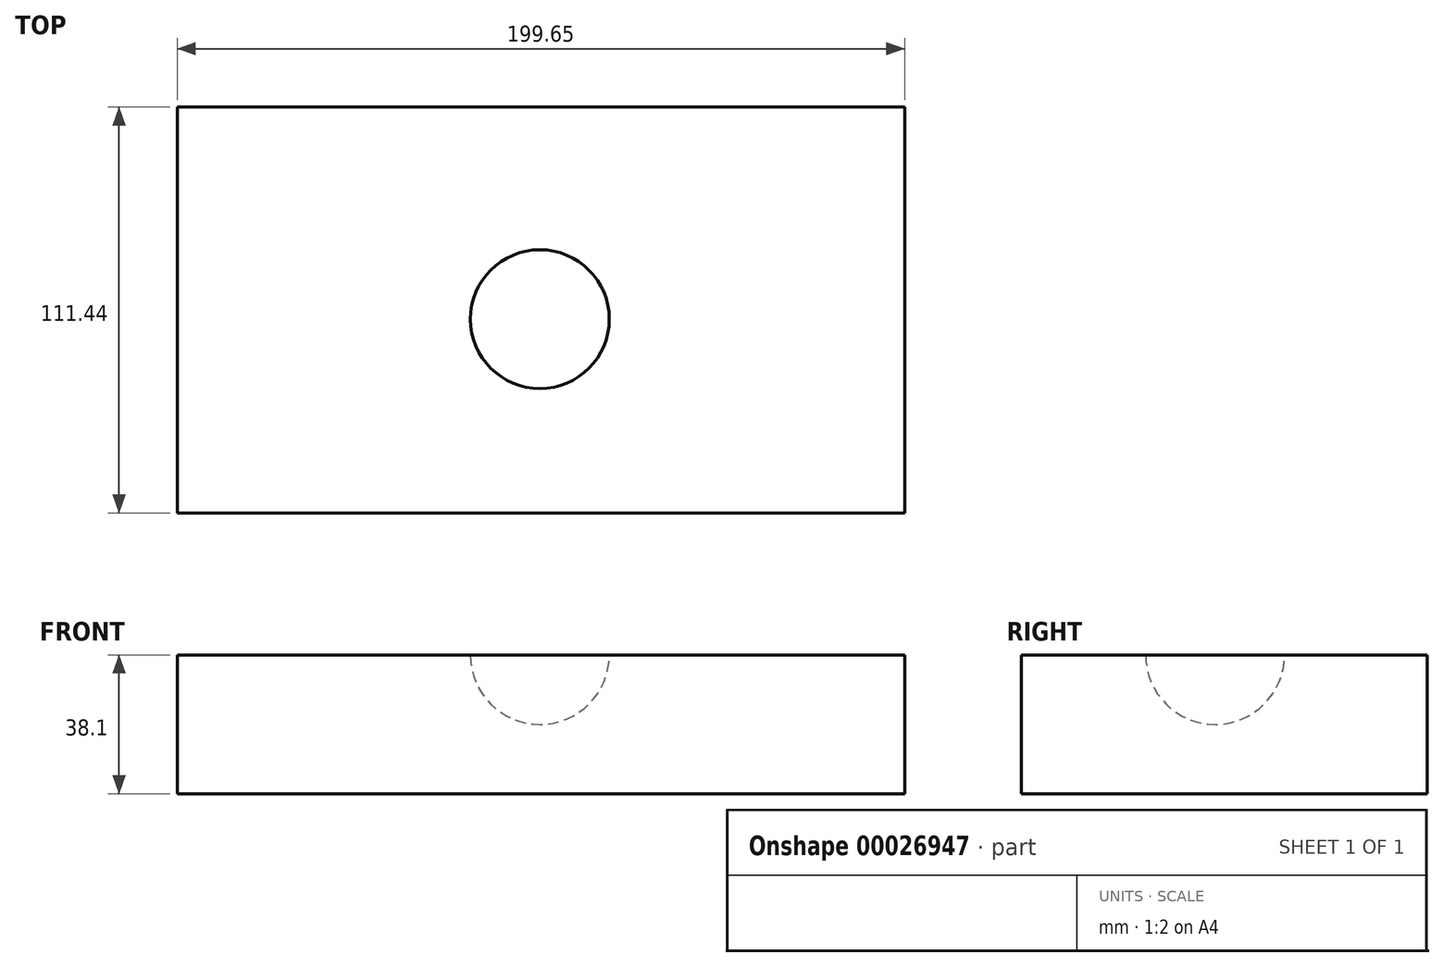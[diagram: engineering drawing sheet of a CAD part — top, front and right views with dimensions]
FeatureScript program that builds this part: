
annotation { "Feature Type Name" : "Feature", "Feature Type Description" : "" }
export const myFeature = defineFeature(function(context is Context, id is Id, definition is map)
    precondition{}
    {
        {
            var Q0;
            Q0=qCreatedBy(makeId("Top.planeOp"),FACE);
            var sketch = newSketch(context, id + "F0", { "sketchPlane" : qUnion([Q0])});
            skLineSegment(sketch, "E0.bottom", {"start": v(-99.53, 55.87) * mm, "end": v(100.12, 55.87) * mm});
            skLineSegment(sketch, "E0.top", {"start": v(-99.53, -55.57) * mm, "end": v(100.12, -55.57) * mm});
            skLineSegment(sketch, "E0.left", {"start": v(-99.53, 55.87) * mm, "end": v(-99.53, -55.57) * mm});
            skLineSegment(sketch, "E0.right", {"start": v(100.12, 55.87) * mm, "end": v(100.12, -55.57) * mm});
            skSolve(sketch);
        }
        {
            var Q0;
            Q0 = qSketchRegion(id + "F0", true);
            extrude(context, id + "F1", {"entities" : qUnion([Q0]), "depth" : 38.1 * mm});
        }
        {
            var Q0;
            Q0=qCreatedBy(makeId("Top.planeOp"),FACE);
            cPlane(context, id + "F2", {"entities" : qUnion([Q0]), "cplaneType" : CPlaneType.OFFSET, "offset" : 38.1 * mm, "width" : 152.4 * mm, "height" : 152.4 * mm});
        }
        {
            var Q0;
            Q0=qCreatedBy(id+"F2.planeOp",FACE);
            var sketch = newSketch(context, id + "F3", { "sketchPlane" : qUnion([Q0])});
            skLineSegment(sketch, "E1", {"start": v(0, 16.7) * mm, "end": v(0, -21.4) * mm});
            skArc(sketch, "E2", {"start": v(0, -21.4) * mm, "mid": v(19.05, -2.36) * mm, "end": v(0, 16.7) * mm});
            skSolve(sketch);
        }
        {
            var Q0;
            Q0 = qSketchRegion(id + "F3", true);
            var Q1;
            Q1=sQuery(id+"F3.wireOp",EDGE,"E1");
            revolve(context, id + "F4", {"operationType" : NewBodyOperationType.REMOVE, "entities" : qUnion([Q0]), "axis" : qUnion([Q1]), "revolveType" : RevolveType.FULL, "oppositeDirection" : true});
        }
    });
